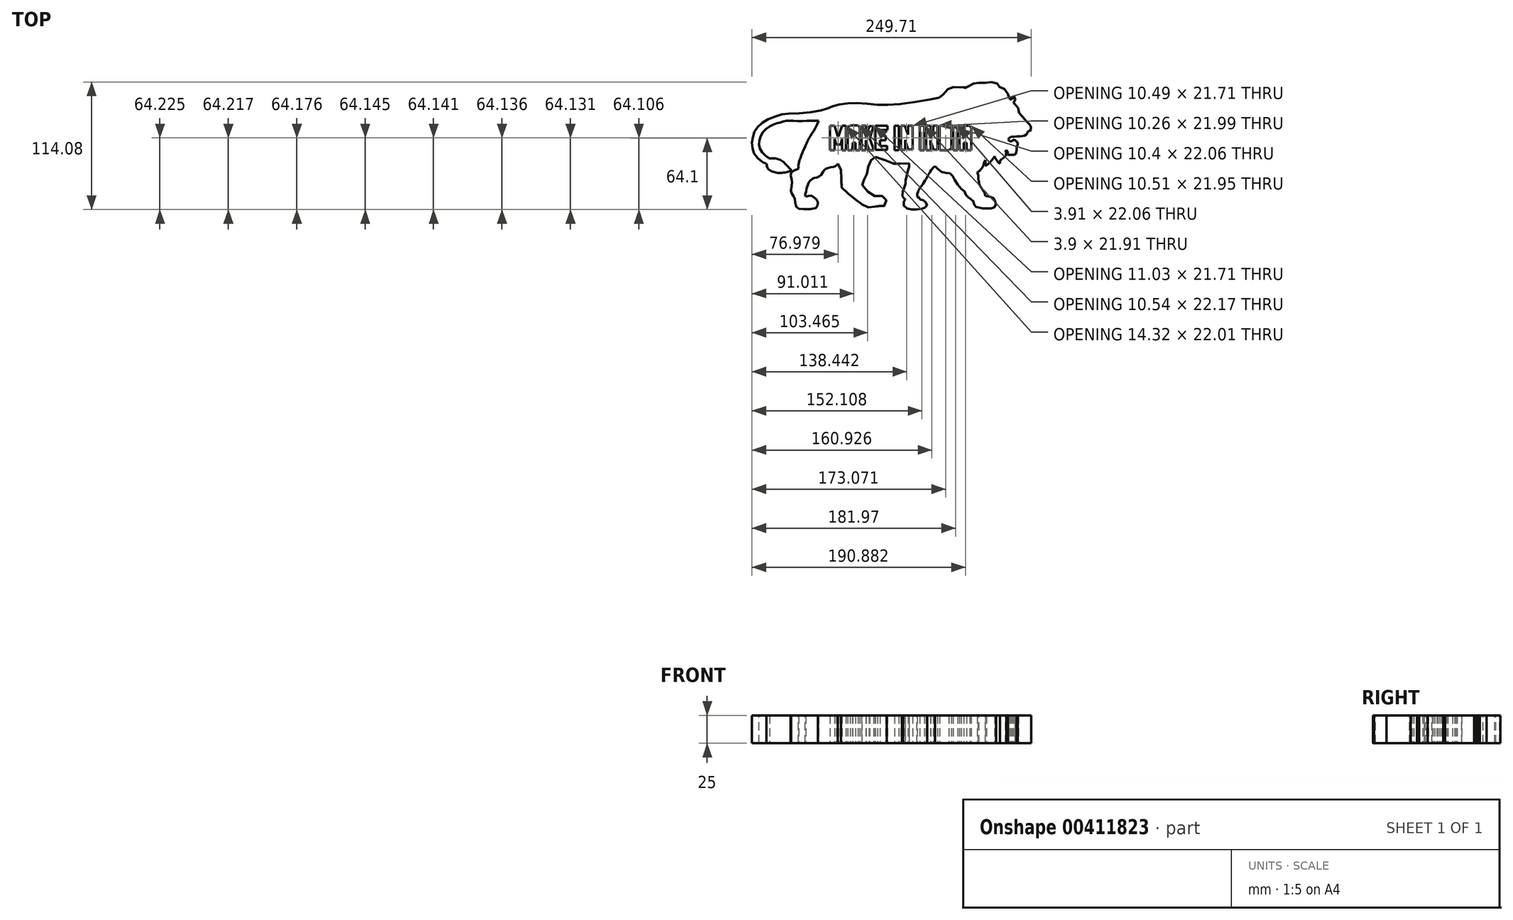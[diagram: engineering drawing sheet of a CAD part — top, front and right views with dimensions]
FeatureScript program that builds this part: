
annotation { "Feature Type Name" : "Feature", "Feature Type Description" : "" }
export const myFeature = defineFeature(function(context is Context, id is Id, definition is map)
    precondition{}
    {
        {
            var Q0;
            Q0=qCreatedBy(makeId("Top.planeOp"),FACE);
            var sketch = newSketch(context, id + "F0", { "sketchPlane" : qUnion([Q0])});
            skFitSpline(sketch, "E0", {"points": [v(-18.47, 30.71) * mm, v(-9.54, 30.43) * mm, v(3.86, 31.41) * mm, v(24.52, 34.62) * mm, v(35.37, 36.55) * mm, v(37.36, 37.42) * mm, v(39.06, 38.5) * mm, v(42.14, 42.2) * mm, v(44.63, 44.68) * mm, v(46.66, 45.64) * mm, v(51.56, 46.63) * mm, v(56.29, 46.22) * mm, v(59.77, 45.72) * mm, v(62.22, 47.09) * mm, v(67.24, 49.41) * mm, v(69.57, 50.12) * mm, v(72.47, 50.12) * mm, v(76.25, 50.04) * mm, v(79.53, 50.4) * mm, v(82.43, 50.82) * mm, v(85.3, 50.7) * mm, v(88.04, 49.87) * mm, v(89.61, 48.13) * mm, v(90.03, 46.92) * mm, v(92.06, 45.88) * mm, v(93.93, 45.35) * mm, v(95.84, 43.9) * mm, v(97.58, 40.9) * mm, v(98.16, 39.37) * mm, v(97.87, 38.75) * mm, v(98.66, 37.75) * mm, v(98.79, 36.88) * mm, v(98.9, 36.13) * mm, v(100.03, 35.26) * mm, v(102.06, 35.6) * mm, v(103.56, 37.25) * mm, v(104.22, 38.5) * mm, v(104.6, 36.84) * mm, v(104.51, 34.02) * mm, v(103.97, 33.06) * mm, v(102.98, 32.27) * mm], "startDerivative": vector(202.03, -10.64) * mm, "endDerivative": vector(-67.3, -47.71) * mm});
            skLineSegment(sketch, "E1", {"start": v(102.98, 32.27) * mm, "end": v(104.25, 31.24) * mm});
            skLineSegment(sketch, "E2", {"start": v(104.25, 31.24) * mm, "end": v(104.87, 30.53) * mm});
            skLineSegment(sketch, "E3", {"start": v(104.87, 30.53) * mm, "end": v(105.32, 29.92) * mm});
            skLineSegment(sketch, "E4", {"start": v(105.32, 29.92) * mm, "end": v(105.62, 29.47) * mm});
            skLineSegment(sketch, "E5", {"start": v(105.62, 29.47) * mm, "end": v(106.12, 28.87) * mm});
            skLineSegment(sketch, "E6", {"start": v(106.12, 28.87) * mm, "end": v(106.6, 28.32) * mm});
            skLineSegment(sketch, "E7", {"start": v(106.6, 28.32) * mm, "end": v(107.01, 27.86) * mm});
            skLineSegment(sketch, "E8", {"start": v(107.01, 27.86) * mm, "end": v(107.38, 27.31) * mm});
            skFitSpline(sketch, "E9", {"points": [v(107.38, 27.31) * mm, v(107.55, 26.73) * mm, v(107.51, 25.68) * mm, v(107.79, 24.54) * mm, v(108.01, 23.46) * mm, v(108.73, 22.41) * mm, v(109.74, 21.31) * mm, v(110.82, 20.23) * mm, v(112.12, 18.75) * mm, v(114.8, 15.54) * mm, v(116.82, 13.44) * mm, v(118.5, 11.45) * mm, v(118.63, 8.52) * mm, v(117.17, 7.06) * mm, v(115.6, 6.46) * mm, v(115.18, 4.68) * mm, v(114.39, 3.94) * mm, v(112.93, 3) * mm, v(111.67, 2.54) * mm, v(107.77, 2.39) * mm, v(104.2, 2.14) * mm, v(101.38, 1.9) * mm, v(99.73, 1.33) * mm], "startDerivative": vector(9.4, -20.99) * mm, "endDerivative": vector(-35.26, -15.16) * mm});
            skLineSegment(sketch, "E10", {"start": v(99.73, 1.33) * mm, "end": v(98.99, 0.61) * mm});
            skLineSegment(sketch, "E11", {"start": v(98.99, 0.61) * mm, "end": v(98.62, -0.47) * mm});
            skLineSegment(sketch, "E12", {"start": v(98.62, -0.47) * mm, "end": v(98.99, -1.46) * mm});
            skLineSegment(sketch, "E13", {"start": v(98.99, -1.46) * mm, "end": v(99.83, -2.05) * mm});
            skLineSegment(sketch, "E14", {"start": v(99.83, -2.05) * mm, "end": v(100.91, -2.05) * mm});
            skLineSegment(sketch, "E15", {"start": v(100.91, -2.05) * mm, "end": v(102.12, -1.44) * mm});
            skLineSegment(sketch, "E16", {"start": v(102.12, -1.44) * mm, "end": v(102.62, -1.07) * mm});
            skLineSegment(sketch, "E17", {"start": v(102.62, -1.07) * mm, "end": v(102.8, -0.45) * mm});
            skFitSpline(sketch, "E18", {"points": [v(102.8, -0.45) * mm, v(104.2, -1.02) * mm, v(106.12, -2.5) * mm, v(106.76, -3.83) * mm, v(106.52, -5.63) * mm, v(105.8, -6.86) * mm, v(105.7, -8.02) * mm, v(105.75, -9.75) * mm, v(105.23, -12.76) * mm, v(104.17, -13.85) * mm, v(102.3, -14.24) * mm, v(99.63, -14.17) * mm, v(97.93, -13.87) * mm], "startDerivative": vector(17.55, -5.65) * mm, "endDerivative": vector(-12.58, 12.96) * mm});
            skFitSpline(sketch, "E19", {"points": [v(97.93, -13.87) * mm, v(97.93, -12.36) * mm, v(97.93, -11.6) * mm, v(96.93, -10.63) * mm, v(95.94, -10.57) * mm, v(96.32, -11.51) * mm, v(96.4, -13.87) * mm, v(95.61, -15.62) * mm, v(92.7, -17.94) * mm, v(91.24, -19.14) * mm, v(90.77, -20.6) * mm, v(90.89, -21.87) * mm], "startDerivative": vector(-0.69, 18.64) * mm, "endDerivative": vector(2.68, -15) * mm});
            skFitSpline(sketch, "E20", {"points": [v(86.18, -15.39) * mm, v(86.82, -17.07) * mm, v(88.38, -19.63) * mm, v(89.86, -21.4) * mm, v(90.89, -21.87) * mm], "startDerivative": vector(2.18, -6.74) * mm, "endDerivative": vector(5.49, -1.66) * mm});
            skFitSpline(sketch, "E21", {"points": [v(86.18, -15.39) * mm, v(85.2, -16.96) * mm, v(83.56, -19.14) * mm, v(81.61, -21.11) * mm, v(79.55, -23.2) * mm, v(78.78, -23.73) * mm], "startDerivative": vector(-4.85, -8.12) * mm, "endDerivative": vector(-5.27, -2.98) * mm});
            skFitSpline(sketch, "E22", {"points": [v(78.78, -23.73) * mm, v(78.16, -23.73) * mm, v(78.02, -21.87) * mm, v(77.91, -18.85) * mm], "startDerivative": vector(-3.61, -0.98) * mm, "endDerivative": vector(-0.44, 6.71) * mm});
            skFitSpline(sketch, "E23", {"points": [v(77.91, -18.85) * mm, v(76.68, -21.42) * mm, v(75.77, -24.56) * mm, v(74.45, -26.58) * mm, v(73.26, -27.8) * mm, v(72.04, -28.99) * mm, v(70.6, -29.62) * mm], "startDerivative": vector(-7.25, -12.85) * mm, "endDerivative": vector(-10.66, -3.5) * mm});
            skFitSpline(sketch, "E24", {"points": [v(70.6, -29.62) * mm, v(71.52, -32.18) * mm, v(71.47, -35.54) * mm, v(72.17, -39) * mm, v(72.21, -40.28) * mm, v(73.55, -42.4) * mm, v(74.98, -44.92) * mm, v(76.46, -47.09) * mm, v(77.45, -49.31) * mm, v(77.91, -51.04) * mm], "startDerivative": vector(10.6, -21.47) * mm, "endDerivative": vector(4.25, -17.87) * mm});
            skFitSpline(sketch, "E25", {"points": [v(77.91, -51.04) * mm, v(81.85, -51.57) * mm, v(85.06, -52.83) * mm, v(86.18, -55.27) * mm, v(87.22, -56.8) * mm, v(87.36, -59.32) * mm, v(85.62, -61.55) * mm, v(83.45, -62.11) * mm, v(71.1, -61.41) * mm, v(68.38, -59.6) * mm, v(67.68, -57.71) * mm, v(67.15, -55.47) * mm, v(65.4, -54.1) * mm, v(63.45, -52.82) * mm, v(61.84, -51.77) * mm, v(60.34, -49.7) * mm, v(59.26, -47.09) * mm, v(56.68, -44.79) * mm, v(52.35, -39.76) * mm, v(49.39, -34.77) * mm, v(48.16, -32.4) * mm, v(45.51, -30.51) * mm, v(42.34, -30.41) * mm, v(38, -29.01) * mm, v(34.03, -25.56) * mm, v(32.8, -24.3) * mm], "startDerivative": vector(88.82, -10.43) * mm, "endDerivative": vector(-35.41, 36.47) * mm});
            skFitSpline(sketch, "E26", {"points": [v(32.8, -24.3) * mm, v(30.23, -26.82) * mm, v(27.05, -31.88) * mm, v(24.5, -36.45) * mm, v(20.28, -42.7) * mm, v(17.87, -46.67) * mm, v(16.8, -50.48) * mm, v(16.86, -51.53) * mm], "startDerivative": vector(-20.03, -16.79) * mm, "endDerivative": vector(2.33, -16.53) * mm});
            skFitSpline(sketch, "E27", {"points": [v(16.86, -51.53) * mm, v(17.94, -51.53) * mm, v(18.6, -52.68) * mm, v(19.4, -53.51) * mm, v(19.76, -54.39) * mm, v(21.36, -54.7) * mm, v(23.46, -55.57) * mm, v(24.85, -56.83) * mm, v(25.27, -57.63) * mm, v(25.62, -60.04) * mm, v(24.12, -61.33) * mm, v(21.89, -62.34) * mm, v(16.86, -63.04) * mm, v(12.29, -63.18) * mm, v(7.93, -62.1) * mm, v(5, -59.8) * mm, v(4.5, -56.8) * mm, v(5.66, -54.73) * mm, v(6.29, -54.18) * mm, v(6.29, -53.69) * mm, v(5.17, -53.16) * mm, v(4.05, -52.54) * mm, v(3.46, -50.76) * mm, v(3.84, -47.09) * mm, v(4.89, -44.4) * mm, v(6.4, -40.78) * mm, v(6.4, -37.74) * mm, v(6.95, -35.26) * mm, v(7.5, -32.54) * mm, v(9.18, -26.78) * mm, v(9.81, -24.3) * mm, v(9.7, -21.87) * mm], "startDerivative": vector(53.79, 7.99) * mm, "endDerivative": vector(-7.67, 75.84) * mm});
            skFitSpline(sketch, "E28", {"points": [v(9.7, -21.87) * mm, v(3.47, -21.87) * mm, v(-0.52, -22.16) * mm, v(-1.54, -21.52) * mm, v(-4.65, -22.08) * mm, v(-8.53, -20.6) * mm, v(-18.18, -16.68) * mm, v(-20.65, -16.24) * mm, v(-22.47, -16.65) * mm, v(-24, -18.4) * mm, v(-25.34, -20.87) * mm, v(-26.52, -23.73) * mm, v(-27.08, -26.27) * mm, v(-27.93, -30.8) * mm, v(-28.95, -33.37) * mm, v(-30.33, -35.78) * mm, v(-31.64, -37.57) * mm, v(-32.18, -38.95) * mm, v(-32.23, -41.66) * mm, v(-29.07, -45.76) * mm, v(-24.38, -49.56) * mm, v(-21.42, -51.04) * mm, v(-17.18, -51.04) * mm, v(-14.56, -51.04) * mm, v(-12.29, -52.87) * mm, v(-11.06, -54.35) * mm, v(-10.41, -57.56) * mm, v(-12.04, -59.48) * mm, v(-13.72, -59.88) * mm, v(-20.73, -60.42) * mm, v(-23.34, -61.06) * mm, v(-26.7, -61.16) * mm, v(-29.9, -60.86) * mm, v(-32.13, -58.84) * mm, v(-34.4, -56.67) * mm, v(-39.63, -53.36) * mm, v(-44.02, -49.61) * mm, v(-49.06, -45.17) * mm, v(-50.98, -42.9) * mm, v(-51.38, -38.7) * mm, v(-50.79, -31.7) * mm, v(-51.28, -27.35) * mm, v(-52.41, -24.2) * mm, v(-54.1, -22.27) * mm], "startDerivative": vector(-204, 11.4) * mm, "endDerivative": vector(-92.33, 87.9) * mm});
            skFitSpline(sketch, "E29", {"points": [v(-54.1, -22.27) * mm, v(-55.47, -23.6) * mm, v(-57.25, -24.88) * mm, v(-62.24, -25.72) * mm, v(-65.1, -26.9) * mm, v(-67.02, -28.93) * mm, v(-68.55, -31.55) * mm, v(-71.61, -33.96) * mm, v(-75.46, -35.05) * mm, v(-79.26, -37.77) * mm, v(-80.74, -40.58) * mm, v(-81.68, -43.4) * mm, v(-82.72, -47.78) * mm, v(-83.3, -50.48) * mm, v(-82.82, -51.53) * mm], "startDerivative": vector(-25.32, -23.95) * mm, "endDerivative": vector(21.34, -28.08) * mm});
            skFitSpline(sketch, "E30", {"points": [v(-82.82, -51.53) * mm, v(-80.25, -50.92) * mm, v(-77.98, -50.87) * mm, v(-74.87, -52.65) * mm, v(-72.2, -55.9) * mm, v(-72.25, -58.87) * mm, v(-74.03, -61.88) * mm, v(-86.12, -62.72) * mm, v(-91.06, -61.04) * mm, v(-92.3, -55.61) * mm, v(-93.08, -52.25) * mm, v(-95.2, -48.7) * mm, v(-96, -46.53) * mm, v(-95.25, -39.82) * mm, v(-95.45, -36.46) * mm, v(-96.39, -32.17) * mm, v(-95.4, -29.65) * mm, v(-89.18, -26.69) * mm], "startDerivative": vector(56.3, 14.67) * mm, "endDerivative": vector(99.9, 36.71) * mm});
            skFitSpline(sketch, "E31", {"points": [v(-89.18, -26.69) * mm, v(-89.18, -22.28) * mm, v(-87.2, -15.9) * mm, v(-82.82, -5.52) * mm, v(-80.24, 0) * mm, v(-74.01, 10.25) * mm, v(-71.27, 16.15) * mm], "startDerivative": vector(-2.37, 34.09) * mm, "endDerivative": vector(13.99, 34.57) * mm});
            skFitSpline(sketch, "E32", {"points": [v(-71.27, 16.15) * mm, v(-79.74, 16.15) * mm, v(-92.6, 16.15) * mm, v(-100.07, 16.15) * mm, v(-106.13, 14.74) * mm, v(-113.94, 12) * mm, v(-122.15, 4.44) * mm, v(-124.31, -7.1) * mm, v(-119.75, -14.15) * mm, v(-115.26, -17.39) * mm], "startDerivative": vector(-71.57, 0.29) * mm, "endDerivative": vector(50.11, -31.68) * mm});
            skFitSpline(sketch, "E33", {"points": [v(-115.26, -17.39) * mm, v(-111.03, -17.39) * mm, v(-104.72, -19.3) * mm, v(-99.08, -24.44) * mm, v(-95.5, -28.34) * mm], "startDerivative": vector(18.84, 1.03) * mm, "endDerivative": vector(14.22, -15.44) * mm});
            skFitSpline(sketch, "E34", {"points": [v(-95.5, -28.34) * mm, v(-98.5, -29.34) * mm, v(-105.6, -30.46) * mm, v(-111.45, -29.59) * mm, v(-116.97, -26.1) * mm, v(-117.84, -22.16) * mm], "startDerivative": vector(-16.67, -6.4) * mm, "endDerivative": vector(-0.33, 23.5) * mm});
            skFitSpline(sketch, "E35", {"points": [v(-117.84, -22.16) * mm, v(-119.75, -21.43) * mm, v(-125.18, -18) * mm, v(-129.18, -12.42) * mm, v(-130.53, -7.66) * mm, v(-130.8, -1.91) * mm, v(-129.64, 3.79) * mm, v(-127.74, 8.18) * mm, v(-123.15, 13.17) * mm, v(-116.96, 17.29) * mm, v(-107.24, 21.14) * mm, v(-100.03, 22.5) * mm, v(-79.84, 23.79) * mm, v(-64.24, 26.95) * mm, v(-59.4, 28.92) * mm, v(-51.01, 31.1) * mm, v(-37.3, 32.08) * mm, v(-18.47, 30.71) * mm], "startDerivative": vector(-56.55, 18.8) * mm, "endDerivative": vector(218.28, -21.75) * mm});
            skLineSegment(sketch, "E36", {"start": v(-57.06, -10.09) * mm, "end": v(-61.05, -10.09) * mm});
            skLineSegment(sketch, "E37", {"start": v(-61.05, -10.09) * mm, "end": v(-61.05, 11.92) * mm});
            skLineSegment(sketch, "E38", {"start": v(-61.05, 11.92) * mm, "end": v(-57.18, 11.92) * mm});
            skLineSegment(sketch, "E39", {"start": v(-57.18, 11.92) * mm, "end": v(-54.2, 2.24) * mm});
            skLineSegment(sketch, "E40", {"start": v(-54.2, 2.24) * mm, "end": v(-53.62, 2.24) * mm});
            skLineSegment(sketch, "E41", {"start": v(-53.62, 2.24) * mm, "end": v(-50.47, 11.8) * mm});
            skLineSegment(sketch, "E42", {"start": v(-50.47, 11.8) * mm, "end": v(-46.73, 11.8) * mm});
            skLineSegment(sketch, "E43", {"start": v(-46.73, 11.8) * mm, "end": v(-46.73, -9.98) * mm});
            skLineSegment(sketch, "E44", {"start": v(-46.73, -9.98) * mm, "end": v(-50.42, -9.98) * mm});
            skLineSegment(sketch, "E45", {"start": v(-50.42, -9.98) * mm, "end": v(-50.42, 0) * mm});
            skLineSegment(sketch, "E46", {"start": v(-50.42, 0) * mm, "end": v(-51.78, -5.02) * mm});
            skLineSegment(sketch, "E47", {"start": v(-51.78, -5.02) * mm, "end": v(-55.45, -5.02) * mm});
            skLineSegment(sketch, "E48", {"start": v(-55.45, -5.02) * mm, "end": v(-57.06, 0) * mm});
            skLineSegment(sketch, "E49", {"start": v(-57.06, 0) * mm, "end": v(-57.06, -10.09) * mm});
            skLineSegment(sketch, "E50", {"start": v(-41, -10.09) * mm, "end": v(-45.13, -10.09) * mm});
            skLineSegment(sketch, "E51", {"start": v(-45.13, -10.09) * mm, "end": v(-45.13, 10.2) * mm});
            skLineSegment(sketch, "E52", {"start": v(-45.13, 10.2) * mm, "end": v(-43.03, 12.08) * mm});
            skLineSegment(sketch, "E53", {"start": v(-43.03, 12.08) * mm, "end": v(-36.2, 12.08) * mm});
            skLineSegment(sketch, "E54", {"start": v(-36.2, 12.08) * mm, "end": v(-34.59, 10.12) * mm});
            skLineSegment(sketch, "E55", {"start": v(-34.59, 10.12) * mm, "end": v(-34.59, -10.09) * mm});
            skLineSegment(sketch, "E56", {"start": v(-34.59, -10.09) * mm, "end": v(-38.36, -10.09) * mm});
            skLineSegment(sketch, "E57", {"start": v(-38.36, -10.09) * mm, "end": v(-38.36, -3.56) * mm});
            skLineSegment(sketch, "E58", {"start": v(-38.36, -3.56) * mm, "end": v(-40.87, -3.56) * mm});
            skLineSegment(sketch, "E59", {"start": v(-40.87, -3.56) * mm, "end": v(-41, -10.09) * mm});
            skPoint(sketch, "E60.orphan", {"position": v(-40.66, -10.09) * mm});
            skLineSegment(sketch, "E61", {"start": v(-38.57, 0.27) * mm, "end": v(-41.08, 0.27) * mm});
            skLineSegment(sketch, "E62", {"start": v(-41.08, 0.27) * mm, "end": v(-41.08, 7.87) * mm});
            skLineSegment(sketch, "E63", {"start": v(-41.08, 7.87) * mm, "end": v(-38.57, 7.87) * mm});
            skLineSegment(sketch, "E64", {"start": v(-38.57, 7.87) * mm, "end": v(-38.57, 0.27) * mm});
            skLineSegment(sketch, "E65", {"start": v(-32.92, 11.69) * mm, "end": v(-32.92, -9.95) * mm});
            skLineSegment(sketch, "E66", {"start": v(-32.92, -9.95) * mm, "end": v(-29.01, -9.95) * mm});
            skLineSegment(sketch, "E67", {"start": v(-29.01, -9.95) * mm, "end": v(-29.01, -1.15) * mm});
            skLineSegment(sketch, "E68", {"start": v(-29.01, -1.15) * mm, "end": v(-26.11, -9.98) * mm});
            skLineSegment(sketch, "E69", {"start": v(-26.11, -9.98) * mm, "end": v(-21.9, -9.98) * mm});
            skLineSegment(sketch, "E70", {"start": v(-21.9, -9.98) * mm, "end": v(-25.52, 0.52) * mm});
            skLineSegment(sketch, "E71", {"start": v(-25.52, 0.52) * mm, "end": v(-22.1, 11.65) * mm});
            skLineSegment(sketch, "E72", {"start": v(-22.1, 11.65) * mm, "end": v(-25.97, 11.65) * mm});
            skLineSegment(sketch, "E73", {"start": v(-25.97, 11.65) * mm, "end": v(-28.9, 3.1) * mm});
            skLineSegment(sketch, "E74", {"start": v(-28.9, 3.1) * mm, "end": v(-28.9, 11.72) * mm});
            skLineSegment(sketch, "E75", {"start": v(-28.9, 11.72) * mm, "end": v(-32.92, 11.69) * mm});
            skLineSegment(sketch, "E76", {"start": v(-20.51, -9.88) * mm, "end": v(-20.51, 11.69) * mm});
            skLineSegment(sketch, "E77", {"start": v(-20.51, 11.69) * mm, "end": v(-9.76, 11.69) * mm});
            skLineSegment(sketch, "E78", {"start": v(-9.76, 11.69) * mm, "end": v(-9.76, 7.88) * mm});
            skLineSegment(sketch, "E79", {"start": v(-9.76, 7.88) * mm, "end": v(-16.5, 7.88) * mm});
            skLineSegment(sketch, "E80", {"start": v(-16.5, 7.88) * mm, "end": v(-16.5, 2.92) * mm});
            skLineSegment(sketch, "E81", {"start": v(-16.5, 2.92) * mm, "end": v(-11.4, 2.92) * mm});
            skLineSegment(sketch, "E82", {"start": v(-11.4, 2.92) * mm, "end": v(-11.4, -1.16) * mm});
            skLineSegment(sketch, "E83", {"start": v(-11.4, -1.16) * mm, "end": v(-16.43, -1.16) * mm});
            skLineSegment(sketch, "E84", {"start": v(-16.43, -1.16) * mm, "end": v(-16.43, -6.11) * mm});
            skLineSegment(sketch, "E85", {"start": v(-16.43, -6.11) * mm, "end": v(-9.94, -6.11) * mm});
            skLineSegment(sketch, "E86", {"start": v(-9.94, -6.11) * mm, "end": v(-9.94, -9.88) * mm});
            skLineSegment(sketch, "E87", {"start": v(-9.94, -9.88) * mm, "end": v(-20.51, -9.88) * mm});
            skLineSegment(sketch, "E88.bottom", {"start": v(0.51, 11.77) * mm, "end": v(-3.47, 11.77) * mm});
            skLineSegment(sketch, "E88.top", {"start": v(0.51, -9.94) * mm, "end": v(-3.47, -9.94) * mm});
            skLineSegment(sketch, "E88.left", {"start": v(0.51, 11.77) * mm, "end": v(0.51, -9.94) * mm});
            skLineSegment(sketch, "E88.right", {"start": v(-3.47, 11.77) * mm, "end": v(-3.47, -9.94) * mm});
            skLineSegment(sketch, "E89", {"start": v(2.33, -9.87) * mm, "end": v(2.33, 11.84) * mm});
            skLineSegment(sketch, "E90", {"start": v(2.33, 11.84) * mm, "end": v(5.82, 11.84) * mm});
            skLineSegment(sketch, "E91", {"start": v(5.82, 11.84) * mm, "end": v(8.6, 3.74) * mm});
            skLineSegment(sketch, "E92", {"start": v(8.6, 3.74) * mm, "end": v(8.6, 11.7) * mm});
            skLineSegment(sketch, "E93", {"start": v(8.6, 11.7) * mm, "end": v(12.82, 11.7) * mm});
            skLineSegment(sketch, "E94", {"start": v(12.82, 11.7) * mm, "end": v(12.82, -9.59) * mm});
            skLineSegment(sketch, "E95", {"start": v(12.82, -9.59) * mm, "end": v(8.7, -9.59) * mm});
            skLineSegment(sketch, "E96", {"start": v(8.7, -9.59) * mm, "end": v(6.26, -0.93) * mm});
            skLineSegment(sketch, "E97", {"start": v(6.26, -0.93) * mm, "end": v(6.26, -9.87) * mm});
            skLineSegment(sketch, "E98", {"start": v(6.26, -9.87) * mm, "end": v(2.33, -9.87) * mm});
            skLineSegment(sketch, "E99.bottom", {"start": v(19.29, 11.86) * mm, "end": v(23.19, 11.86) * mm});
            skLineSegment(sketch, "E99.top", {"start": v(19.29, -10.05) * mm, "end": v(23.19, -10.05) * mm});
            skLineSegment(sketch, "E99.left", {"start": v(19.29, 11.86) * mm, "end": v(19.29, -10.05) * mm});
            skLineSegment(sketch, "E99.right", {"start": v(23.19, 11.86) * mm, "end": v(23.19, -10.05) * mm});
            skLineSegment(sketch, "E100", {"start": v(29.04, -10.08) * mm, "end": v(24.93, -10.08) * mm});
            skLineSegment(sketch, "E101", {"start": v(24.93, -10.08) * mm, "end": v(24.93, 11.9) * mm});
            skLineSegment(sketch, "E102", {"start": v(24.93, 11.9) * mm, "end": v(28.83, 11.9) * mm});
            skLineSegment(sketch, "E103", {"start": v(28.83, 11.9) * mm, "end": v(31.14, 3.6) * mm});
            skLineSegment(sketch, "E104", {"start": v(31.14, 3.6) * mm, "end": v(31.14, 11.83) * mm});
            skLineSegment(sketch, "E105", {"start": v(31.14, 11.83) * mm, "end": v(35.19, 11.83) * mm});
            skLineSegment(sketch, "E106", {"start": v(35.19, 11.83) * mm, "end": v(35.19, -9.8) * mm});
            skLineSegment(sketch, "E107", {"start": v(35.19, -9.8) * mm, "end": v(31.56, -9.8) * mm});
            skLineSegment(sketch, "E108", {"start": v(31.56, -9.8) * mm, "end": v(28.83, -1.22) * mm});
            skLineSegment(sketch, "E109", {"start": v(28.83, -1.22) * mm, "end": v(29.04, -10.08) * mm});
            skLineSegment(sketch, "E110", {"start": v(37, -10.08) * mm, "end": v(37, 11.97) * mm});
            skLineSegment(sketch, "E111", {"start": v(37, 11.97) * mm, "end": v(45.1, 11.97) * mm});
            skLineSegment(sketch, "E112", {"start": v(45.1, 11.97) * mm, "end": v(47.4, 9.67) * mm});
            skLineSegment(sketch, "E113", {"start": v(47.4, 9.67) * mm, "end": v(47.4, -8.13) * mm});
            skLineSegment(sketch, "E114", {"start": v(47.4, -8.13) * mm, "end": v(45.3, -10.08) * mm});
            skLineSegment(sketch, "E115", {"start": v(45.3, -10.08) * mm, "end": v(37, -10.08) * mm});
            skLineSegment(sketch, "E116.bottom", {"start": v(43.28, 7.65) * mm, "end": v(40.98, 7.65) * mm});
            skLineSegment(sketch, "E116.top", {"start": v(43.28, -5.9) * mm, "end": v(40.98, -5.9) * mm});
            skLineSegment(sketch, "E116.left", {"start": v(43.28, 7.65) * mm, "end": v(43.28, -5.9) * mm});
            skLineSegment(sketch, "E116.right", {"start": v(40.98, 7.65) * mm, "end": v(40.98, -5.9) * mm});
            skLineSegment(sketch, "E117.bottom", {"start": v(53.05, 11.9) * mm, "end": v(49.15, 11.9) * mm});
            skLineSegment(sketch, "E117.top", {"start": v(53.05, -10.15) * mm, "end": v(49.15, -10.15) * mm});
            skLineSegment(sketch, "E117.left", {"start": v(53.05, 11.9) * mm, "end": v(53.05, -10.15) * mm});
            skLineSegment(sketch, "E117.right", {"start": v(49.15, 11.9) * mm, "end": v(49.15, -10.15) * mm});
            skLineSegment(sketch, "E118.bottom", {"start": v(61.08, 7.79) * mm, "end": v(58.36, 7.79) * mm});
            skLineSegment(sketch, "E118.top", {"start": v(61.08, 0.39) * mm, "end": v(58.36, 0.39) * mm});
            skLineSegment(sketch, "E118.left", {"start": v(61.08, 7.79) * mm, "end": v(61.08, 0.39) * mm});
            skLineSegment(sketch, "E118.right", {"start": v(58.36, 7.79) * mm, "end": v(58.36, 0.39) * mm});
            skLineSegment(sketch, "E119.bottom", {"start": v(63.8, 11.88) * mm, "end": v(56.34, 11.88) * mm});
            skLineSegment(sketch, "E119.top", {"start": v(65.26, -10.07) * mm, "end": v(61.21, -10.07) * mm});
            skLineSegment(sketch, "E119.left", {"start": v(65.26, 10) * mm, "end": v(65.26, -10.07) * mm});
            skLineSegment(sketch, "E119.right", {"start": v(54.76, 10.4) * mm, "end": v(54.76, -10.07) * mm});
            skLineSegment(sketch, "E120", {"start": v(54.76, 10.4) * mm, "end": v(56.34, 11.88) * mm});
            skLineSegment(sketch, "E121", {"start": v(63.8, 11.88) * mm, "end": v(65.26, 10) * mm});
            skLineSegment(sketch, "E122", {"start": v(58.57, -10.07) * mm, "end": v(58.57, -3.56) * mm});
            skLineSegment(sketch, "E123", {"start": v(58.57, -3.56) * mm, "end": v(61.21, -3.56) * mm});
            skLineSegment(sketch, "E124", {"start": v(61.21, -3.56) * mm, "end": v(61.21, -10.07) * mm});
            skLineSegment(sketch, "E125.trimOffspring", {"start": v(58.57, -10.07) * mm, "end": v(54.76, -10.07) * mm});
            skSolve(sketch);
        }
        {
            var Q0;
            Q0=makeQuery(id+"F0.imprint","IMPRINT",FACE,{"disambiguationData":[TD([[makeQuery(id+"F0.imprint","IMPRINT",EDGE,{"derivedFrom":sQuery(id+"F0.wireOp",EDGE,"E0")}),-1.0]])]});
            extrude(context, id + "F1", {"entities" : qUnion([Q0]), "depth" : 25 * mm});
        }
    });
